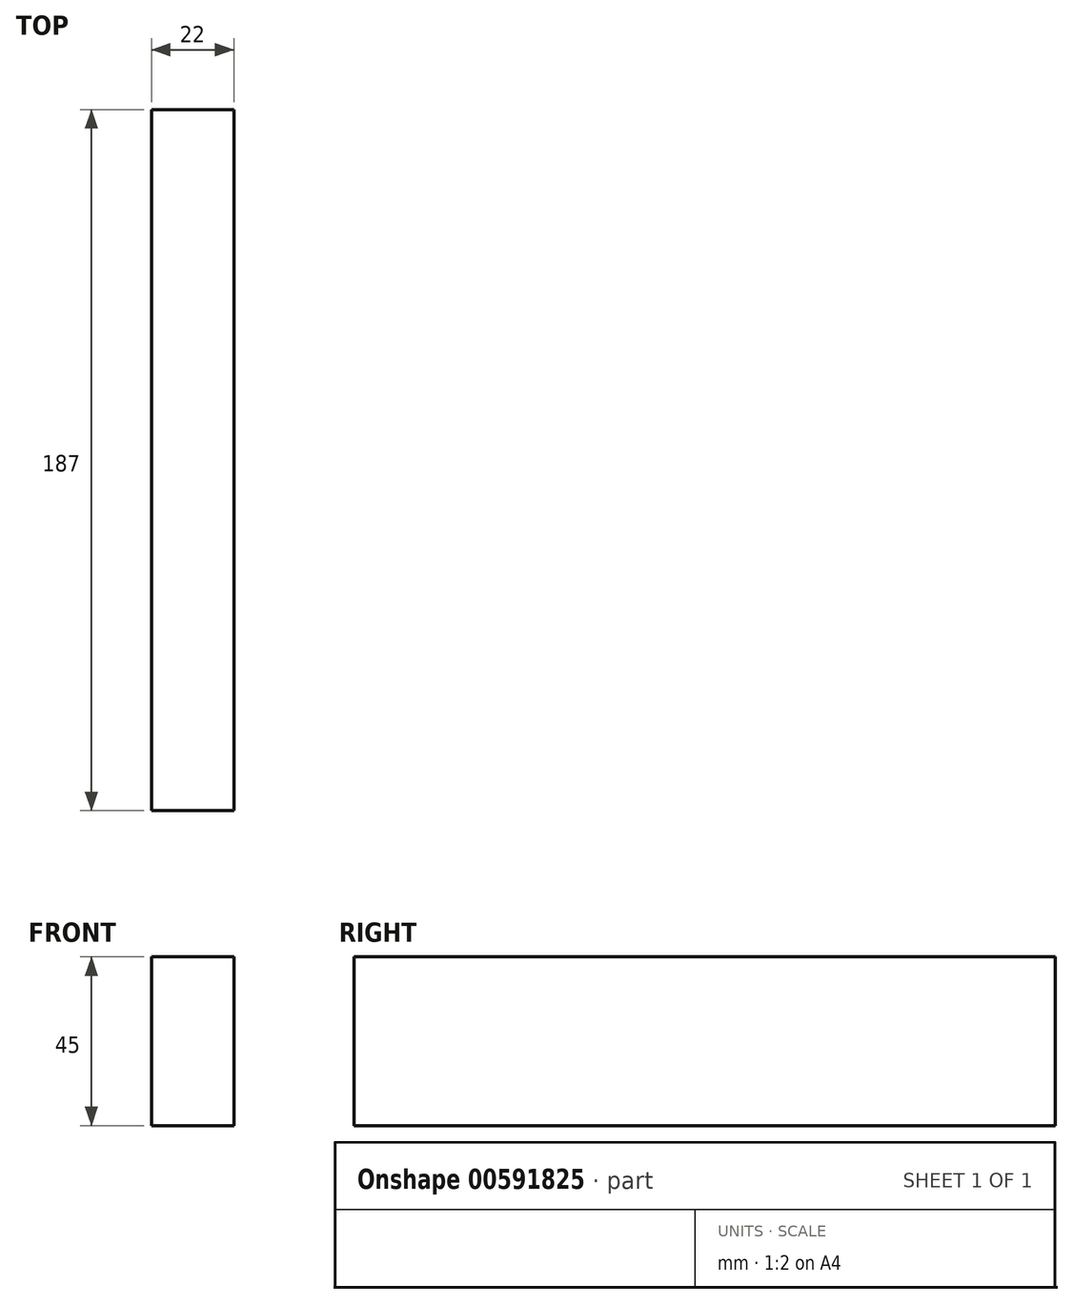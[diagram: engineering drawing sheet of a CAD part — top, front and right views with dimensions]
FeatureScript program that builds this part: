
annotation { "Feature Type Name" : "Feature", "Feature Type Description" : "" }
export const myFeature = defineFeature(function(context is Context, id is Id, definition is map)
    precondition{}
    {
        {
            var Q0;
            Q0=qCreatedBy(makeId("Front.planeOp"),FACE);
            var sketch = newSketch(context, id + "F0", { "sketchPlane" : qUnion([Q0])});
            skLineSegment(sketch, "E0.bottom", {"start": v(0, 0) * mm, "end": v(22, 0) * mm});
            skLineSegment(sketch, "E0.top", {"start": v(0, 45) * mm, "end": v(22, 45) * mm});
            skLineSegment(sketch, "E0.left", {"start": v(0, 0) * mm, "end": v(0, 45) * mm});
            skLineSegment(sketch, "E0.right", {"start": v(22, 0) * mm, "end": v(22, 45) * mm});
            skSolve(sketch);
        }
        {
            var Q0;
            Q0=qSketchRegion(id+"F0",true);
            extrude(context, id + "F1", {"entities" : qUnion([Q0]), "depth" : 187 * mm, "offsetDistance" : 25 * mm});
        }
    });
